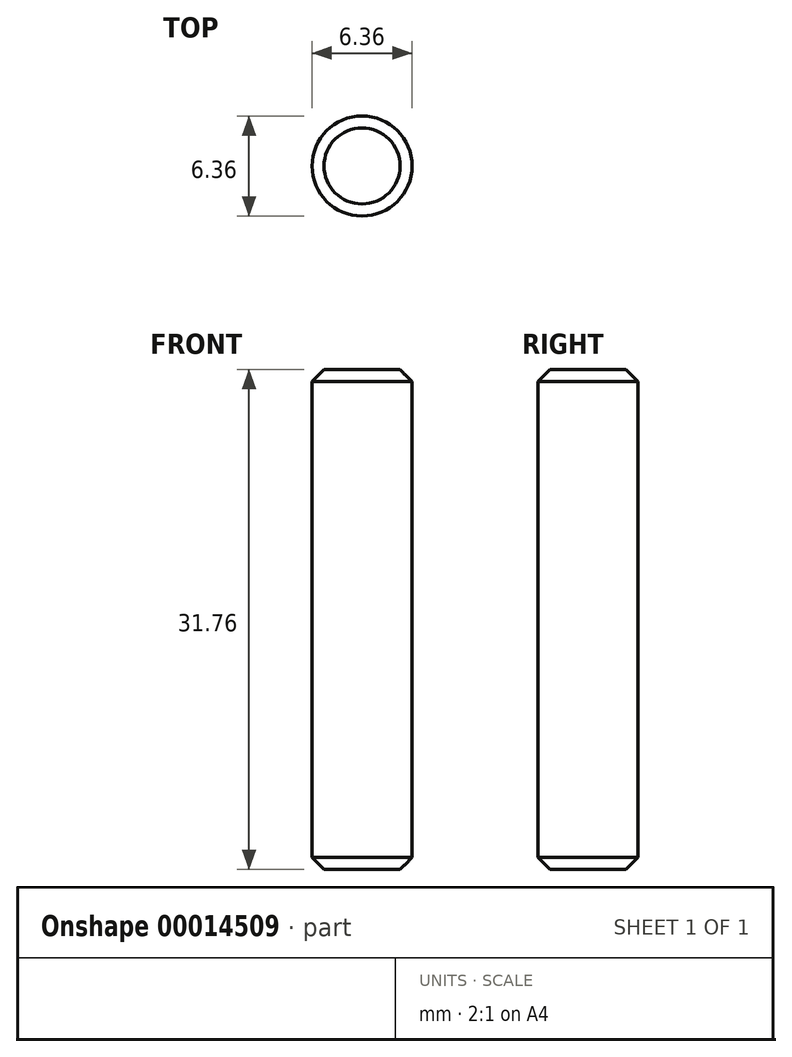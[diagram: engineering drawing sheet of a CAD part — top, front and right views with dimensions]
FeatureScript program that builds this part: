
annotation { "Feature Type Name" : "Feature", "Feature Type Description" : "" }
export const myFeature = defineFeature(function(context is Context, id is Id, definition is map)
    precondition{}
    {
        {
            var Q0;
            Q0=qCreatedBy(makeId("Top.planeOp"),FACE);
            var sketch = newSketch(context, id + "F0", { "sketchPlane" : qUnion([Q0])});
            skCircle(sketch, "E0", {"center": v(0, 0) * mm, "radius": 3.18 * mm});
            skSolve(sketch);
        }
        {
            var Q0;
            Q0 = qSketchRegion(id + "F0", true);
            extrude(context, id + "F1", {"entities" : qUnion([Q0]), "depth" : 31.75 * mm, "symmetric" : true});
        }
        {
            var Q0;
            Q0=makeQuery(id+"F1.opExtrude","CAP_EDGE",EDGE,{"disambiguationData":[OSD([sQuery(id+"F0.wireOp",EDGE,"E0")])],"isStart":false});
            var Q1;
            Q1=makeQuery(id+"F1.opExtrude","CAP_EDGE",EDGE,{"disambiguationData":[OSD([sQuery(id+"F0.wireOp",EDGE,"E0")])],"isStart":true});
            chamfer(context, id + "F2", {"entities" : qUnion([Q0, Q1]), "width" : 0.76 * mm, "tangentPropagation" : true});
        }
    });
